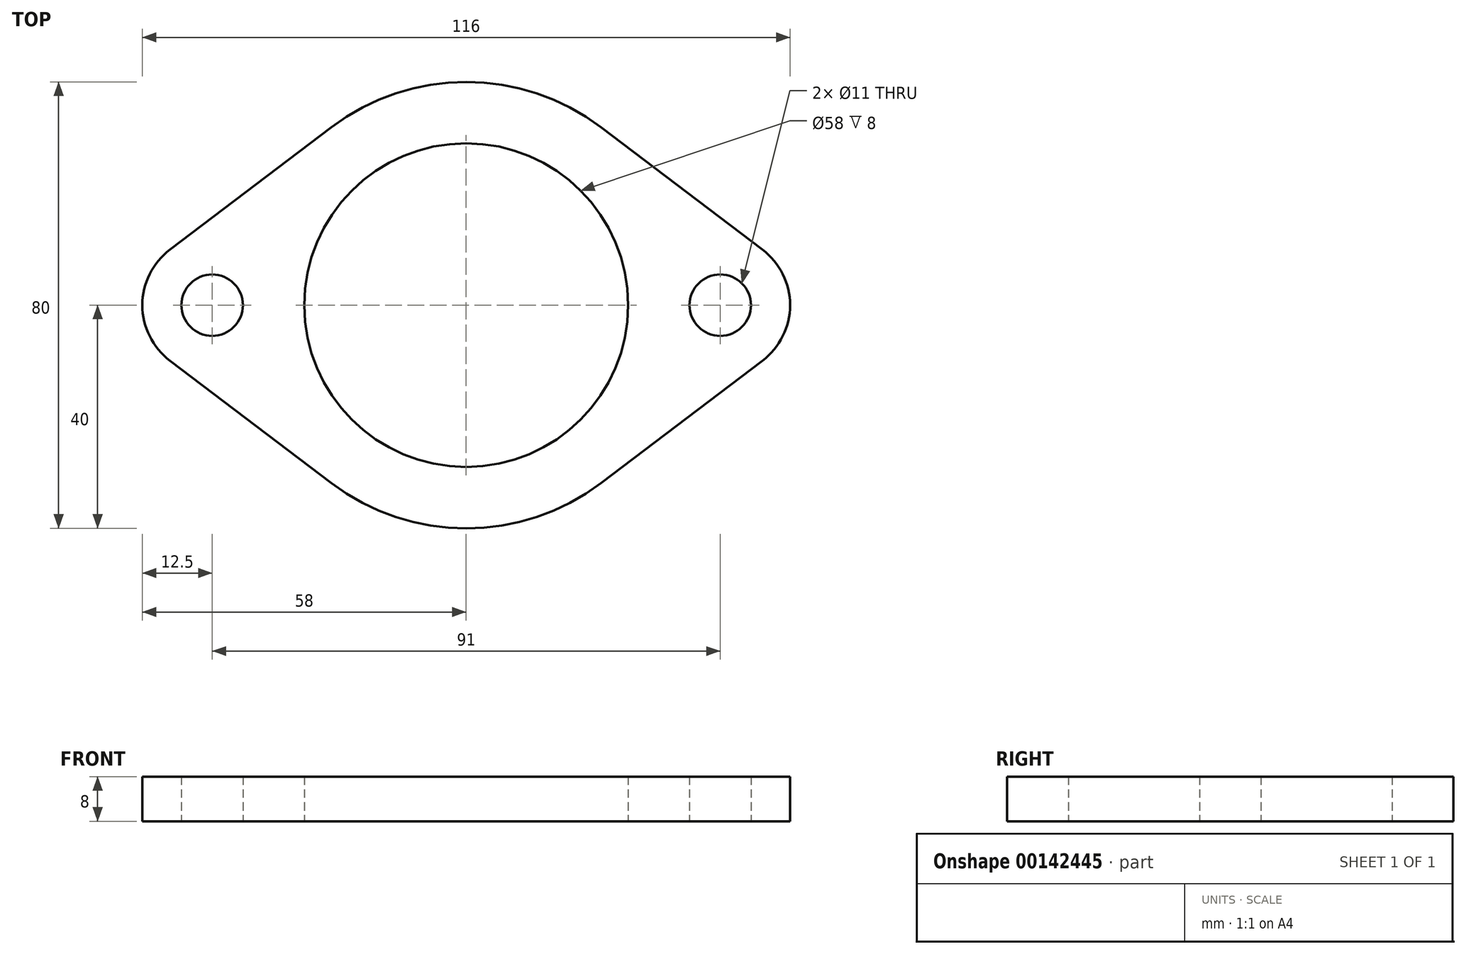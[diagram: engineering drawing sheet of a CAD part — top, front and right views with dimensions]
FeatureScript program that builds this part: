
annotation { "Feature Type Name" : "Feature", "Feature Type Description" : "" }
export const myFeature = defineFeature(function(context is Context, id is Id, definition is map)
    precondition{}
    {
        {
            var Q0;
            Q0=qCreatedBy(makeId("Top.planeOp"),FACE);
            var sketch = newSketch(context, id + "F0", { "sketchPlane" : qUnion([Q0])});
            skCircle(sketch, "E0", {"center": v(0, 0) * mm, "radius": 29 * mm});
            skArc(sketch, "E1", {"start": v(-24.18, -31.87) * mm, "mid": v(0, -40) * mm, "end": v(24.18, -31.87) * mm});
            skCircle(sketch, "E2", {"center": v(-45.5, 0) * mm, "radius": 5.5 * mm});
            skCircle(sketch, "E3", {"center": v(45.5, 0) * mm, "radius": 5.5 * mm});
            skArc(sketch, "E4", {"start": v(-53.05, 9.96) * mm, "mid": v(-58, 0) * mm, "end": v(-53.05, -9.96) * mm});
            skArc(sketch, "E5", {"start": v(53.05, -9.96) * mm, "mid": v(58, 0) * mm, "end": v(53.05, 9.96) * mm});
            skLineSegment(sketch, "E6", {"start": v(-24.18, 31.87) * mm, "end": v(-53.05, 9.96) * mm});
            skLineSegment(sketch, "E7", {"start": v(0, 0) * mm, "end": v(-24.18, 31.87) * mm, "construction": true});
            skLineSegment(sketch, "E8", {"start": v(-45.5, 0) * mm, "end": v(-53.05, 9.96) * mm, "construction": true});
            skLineSegment(sketch, "E9.MirrorCS", {"start": v(24.18, 31.87) * mm, "end": v(53.05, 9.96) * mm});
            skLineSegment(sketch, "E10.MirrorCS", {"start": v(-24.18, -31.87) * mm, "end": v(-53.05, -9.96) * mm});
            skLineSegment(sketch, "E11.MirrorCS", {"start": v(24.18, -31.87) * mm, "end": v(53.05, -9.96) * mm});
            skArc(sketch, "E12.trimOffspring", {"start": v(24.18, 31.87) * mm, "mid": v(0, 40) * mm, "end": v(-24.18, 31.87) * mm});
            skSolve(sketch);
        }
        {
            var Q0;
            Q0=makeQuery(id+"F0.imprint","IMPRINT",FACE,{"disambiguationData":[TD([[makeQuery(id+"F0.imprint","IMPRINT",EDGE,{"derivedFrom":sQuery(id+"F0.wireOp",EDGE,"E0")}),-1.0]])]});
            extrude(context, id + "F1", {"entities" : qUnion([Q0]), "depth" : 8 * mm});
        }
    });
